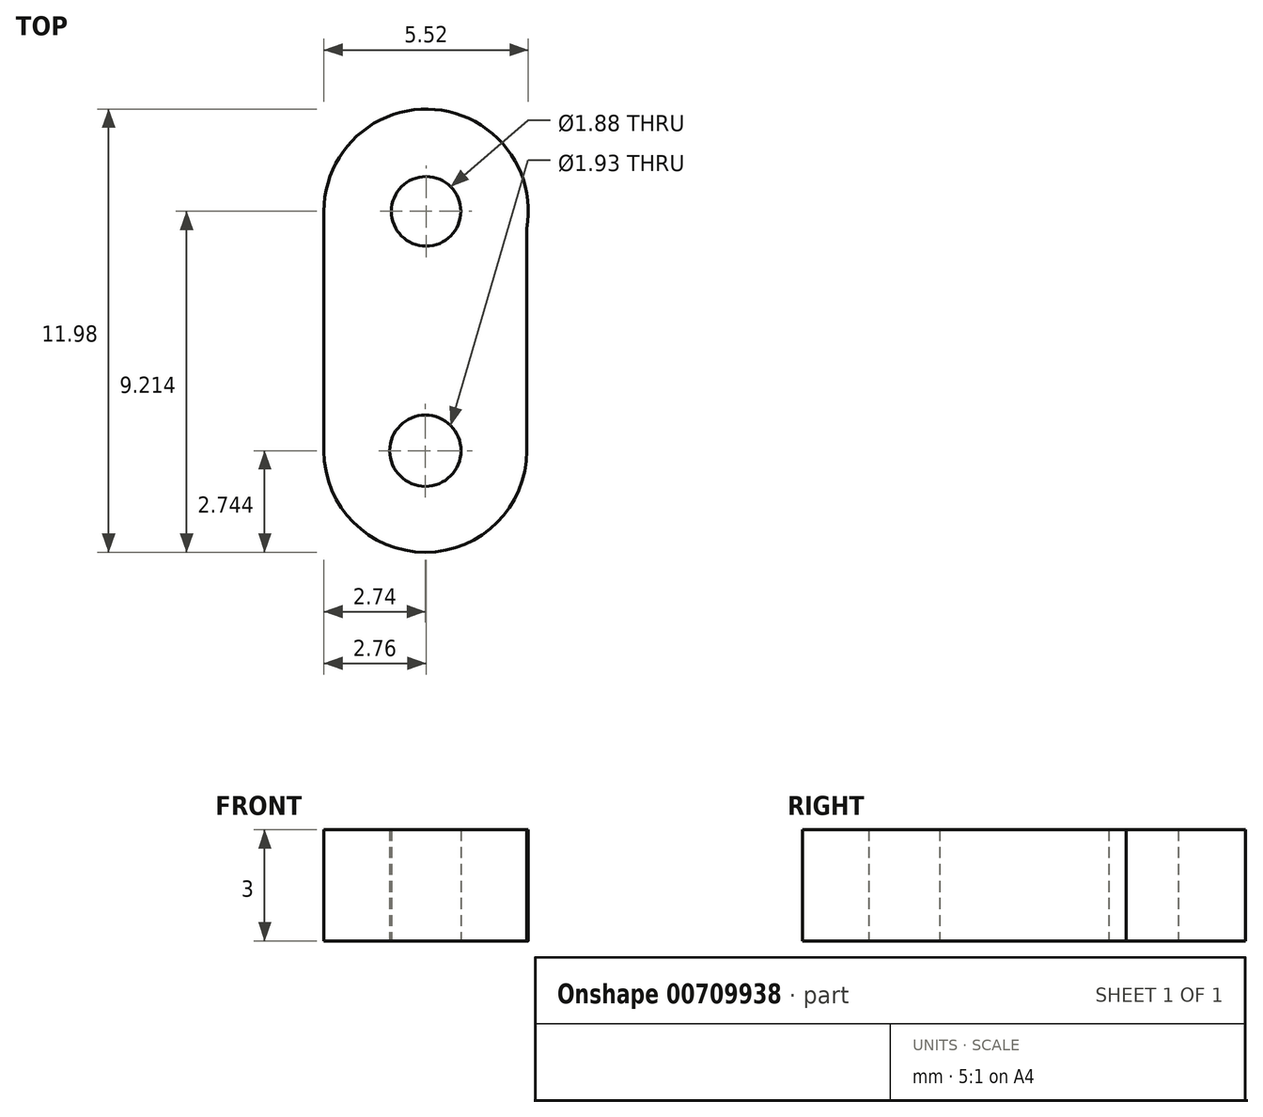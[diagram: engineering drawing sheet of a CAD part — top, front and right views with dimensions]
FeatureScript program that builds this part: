
annotation { "Feature Type Name" : "Feature", "Feature Type Description" : "" }
export const myFeature = defineFeature(function(context is Context, id is Id, definition is map)
    precondition{}
    {
        {
            var Q0;
            Q0=qCreatedBy(makeId("Top.planeOp"),FACE);
            var sketch = newSketch(context, id + "F0", { "sketchPlane" : qUnion([Q0])});
            skLineSegment(sketch, "E0", {"start": v(-2.76, 3.34) * mm, "end": v(-2.76, -3.13) * mm});
            skLineSegment(sketch, "E1", {"start": v(2.72, 2.87) * mm, "end": v(2.72, -3.13) * mm});
            skArc(sketch, "E2", {"start": v(-2.76, 3.34) * mm, "mid": v(0.24, 6.1) * mm, "end": v(2.72, 2.87) * mm});
            skArc(sketch, "E3", {"start": v(-2.76, -3.13) * mm, "mid": v(-0.02, -5.87) * mm, "end": v(2.72, -3.13) * mm});
            skCircle(sketch, "E4", {"center": v(0, 3.34) * mm, "radius": 0.94 * mm});
            skCircle(sketch, "E5", {"center": v(-0.02, -3.13) * mm, "radius": 0.96 * mm});
            skSolve(sketch);
        }
        {
            var Q0;
            Q0=makeQuery(id+"F0.imprint","IMPRINT",FACE,{"disambiguationData":[TD([[makeQuery(id+"F0.imprint","IMPRINT",EDGE,{"derivedFrom":sQuery(id+"F0.wireOp",EDGE,"E0")}),1.0]])]});
            extrude(context, id + "F1", {"entities" : qUnion([Q0]), "depth" : 3 * mm, "offsetDistance" : 25.4 * mm});
        }
    });
